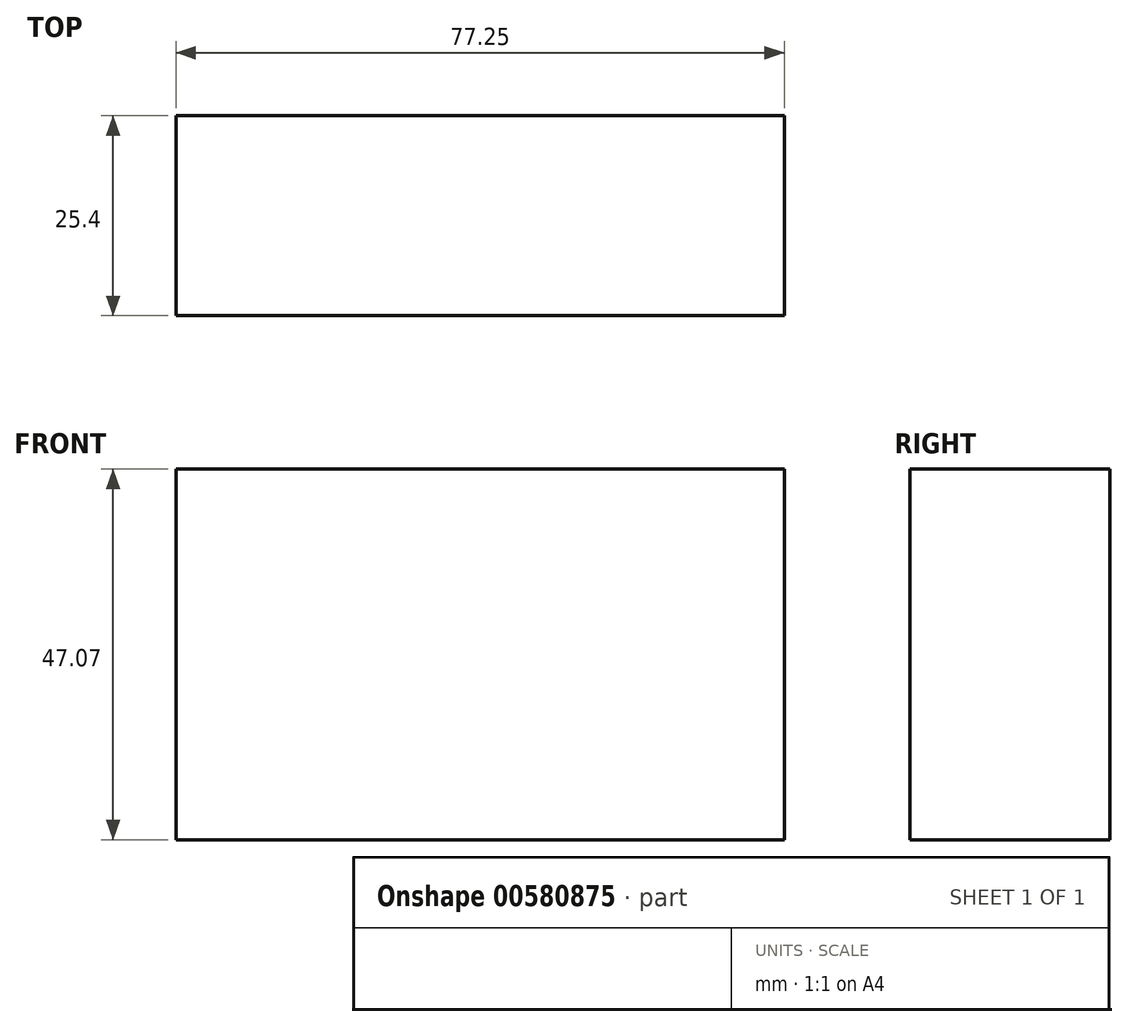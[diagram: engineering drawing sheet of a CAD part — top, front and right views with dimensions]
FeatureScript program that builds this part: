
annotation { "Feature Type Name" : "Feature", "Feature Type Description" : "" }
export const myFeature = defineFeature(function(context is Context, id is Id, definition is map)
    precondition{}
    {
        {
            var Q0;
            Q0=qCreatedBy(makeId("Front.planeOp"),FACE);
            var sketch = newSketch(context, id + "F0", { "sketchPlane" : qUnion([Q0])});
            skLineSegment(sketch, "E0.bottom", {"start": v(0, 0) * mm, "end": v(77.25, 0) * mm});
            skLineSegment(sketch, "E0.top", {"start": v(0, 0) * mm, "end": v(77.25, 0) * mm});
            skLineSegment(sketch, "E0.left", {"start": v(0, 0) * mm, "end": v(0, 0) * mm});
            skLineSegment(sketch, "E0.right", {"start": v(77.25, 0) * mm, "end": v(77.25, 0) * mm});
            skLineSegment(sketch, "E1.bottom", {"start": v(77.25, -47.07) * mm, "end": v(0, -47.07) * mm});
            skLineSegment(sketch, "E1.top", {"start": v(77.25, 0) * mm, "end": v(0, 0) * mm});
            skLineSegment(sketch, "E1.left", {"start": v(77.25, -47.07) * mm, "end": v(77.25, 0) * mm});
            skLineSegment(sketch, "E1.right", {"start": v(0, -47.07) * mm, "end": v(0, 0) * mm});
            skSolve(sketch);
        }
        {
            var Q0;
            Q0 = qSketchRegion(id + "F0", true);
            extrude(context, id + "F1", {"entities" : qUnion([Q0]), "depth" : 25.4 * mm, "offsetDistance" : 25.4 * mm});
        }
    });
